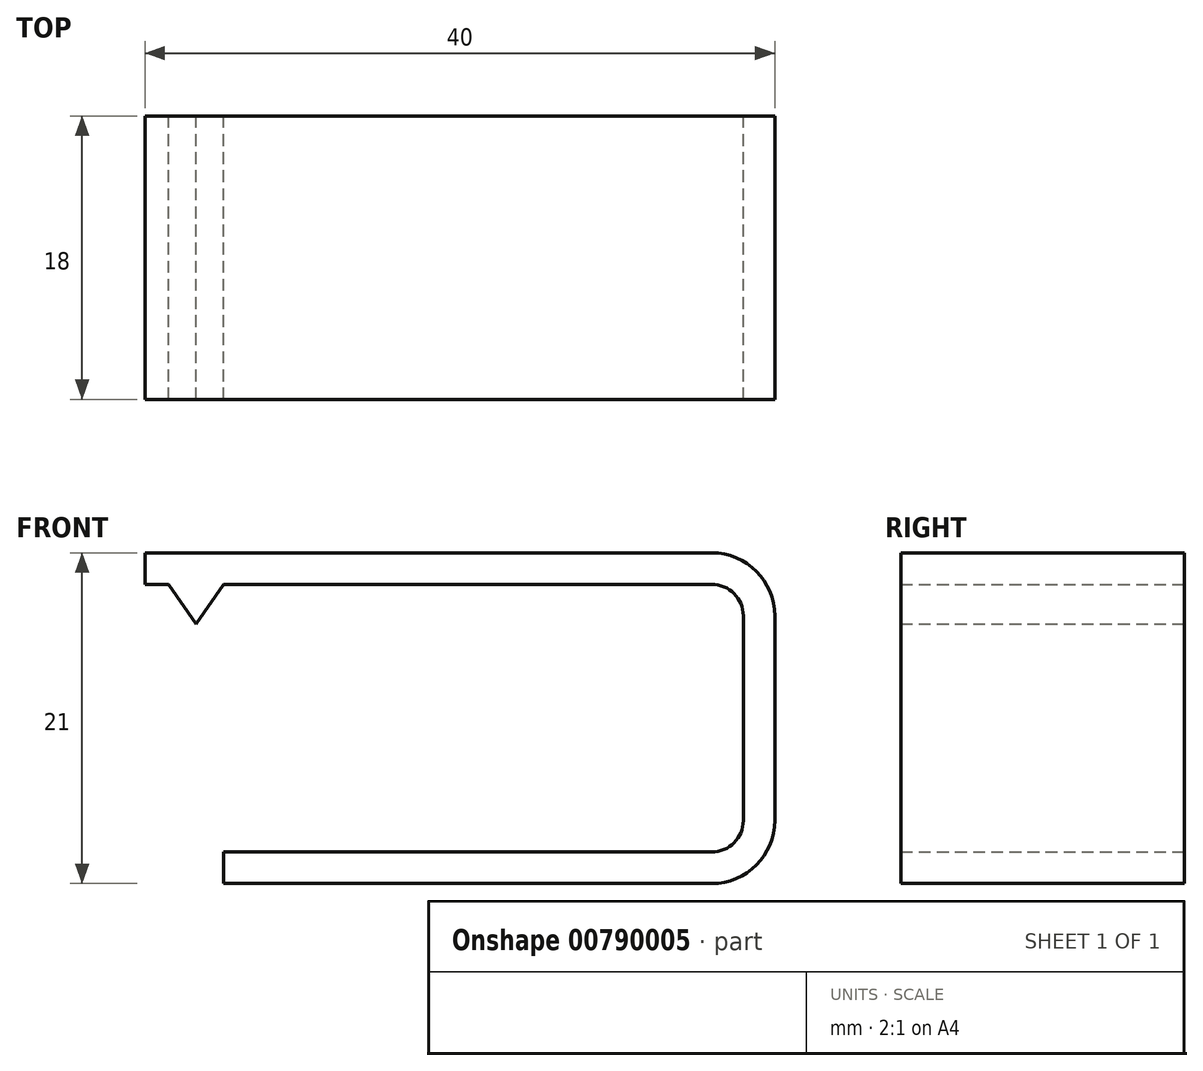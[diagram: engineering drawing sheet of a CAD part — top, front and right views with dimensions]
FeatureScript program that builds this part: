
annotation { "Feature Type Name" : "Feature", "Feature Type Description" : "" }
export const myFeature = defineFeature(function(context is Context, id is Id, definition is map)
    precondition{}
    {
        {
            var Q0;
            Q0=qCreatedBy(makeId("Front.planeOp"),FACE);
            var sketch = newSketch(context, id + "F0", { "sketchPlane" : qUnion([Q0])});
            skLineSegment(sketch, "E0.bottom", {"start": v(16.5, -8.5) * mm, "end": v(-16.5, -8.5) * mm});
            skLineSegment(sketch, "E0.top", {"start": v(16.5, 8.5) * mm, "end": v(-16.5, 8.5) * mm});
            skLineSegment(sketch, "E0.left", {"start": v(16.5, -8.5) * mm, "end": v(16.5, 8.5) * mm});
            skPoint(sketch, "E0.middle", {"position": v(0, 0) * mm});
            skLineSegment(sketch, "E1", {"start": v(-16.5, 8.5) * mm, "end": v(-18.25, 6) * mm});
            skLineSegment(sketch, "E2", {"start": v(-18.25, 6) * mm, "end": v(-20, 8.5) * mm});
            skLineSegment(sketch, "E3", {"start": v(-20, 8.5) * mm, "end": v(-21.5, 8.5) * mm});
            skLineSegment(sketch, "E4", {"start": v(-21.5, 8.5) * mm, "end": v(-21.5, 10.5) * mm});
            skLineSegment(sketch, "E5", {"start": v(-21.5, 10.5) * mm, "end": v(18.5, 10.5) * mm});
            skLineSegment(sketch, "E6", {"start": v(18.5, 10.5) * mm, "end": v(18.5, -10.5) * mm});
            skLineSegment(sketch, "E7", {"start": v(18.5, -10.5) * mm, "end": v(-16.5, -10.5) * mm});
            skLineSegment(sketch, "E8", {"start": v(-16.5, -10.5) * mm, "end": v(-16.5, -8.5) * mm});
            skSolve(sketch);
        }
        {
            var Q0;
            Q0 = qSketchRegion(id + "F0", true);
            extrude(context, id + "F1", {"entities" : qUnion([Q0]), "depth" : 18 * mm, "offsetDistance" : 25 * mm});
        }
        {
            var Q0;
            Q0=makeQuery(id+"F1.opExtrude","SWEPT_EDGE",EDGE,{"disambiguationData":[OSD([sQuery(id+"F0.wireOp",EDGE,"E0.top"),sQuery(id+"F0.wireOp",EDGE,"E0.left")])]});
            var Q1;
            Q1=makeQuery(id+"F1.opExtrude","SWEPT_EDGE",EDGE,{"disambiguationData":[OSD([sQuery(id+"F0.wireOp",EDGE,"E0.bottom"),sQuery(id+"F0.wireOp",EDGE,"E0.left")])]});
            fillet(context, id + "F2", {"entities" : qUnion([Q0, Q1]), "radius" : 2 * mm, "tangentPropagation" : true, "allowEdgeOverflow" : false});
        }
        {
            var Q0;
            Q0=makeQuery(id+"F1.opExtrude","SWEPT_EDGE",EDGE,{"disambiguationData":[OSD([sQuery(id+"F0.wireOp",EDGE,"E5"),sQuery(id+"F0.wireOp",EDGE,"E6")])]});
            var Q1;
            Q1=makeQuery(id+"F1.opExtrude","SWEPT_EDGE",EDGE,{"disambiguationData":[OSD([sQuery(id+"F0.wireOp",EDGE,"E6"),sQuery(id+"F0.wireOp",EDGE,"E7")])]});
            fillet(context, id + "F3", {"entities" : qUnion([Q0, Q1]), "radius" : 4 * mm, "tangentPropagation" : true, "allowEdgeOverflow" : false});
        }
    });
